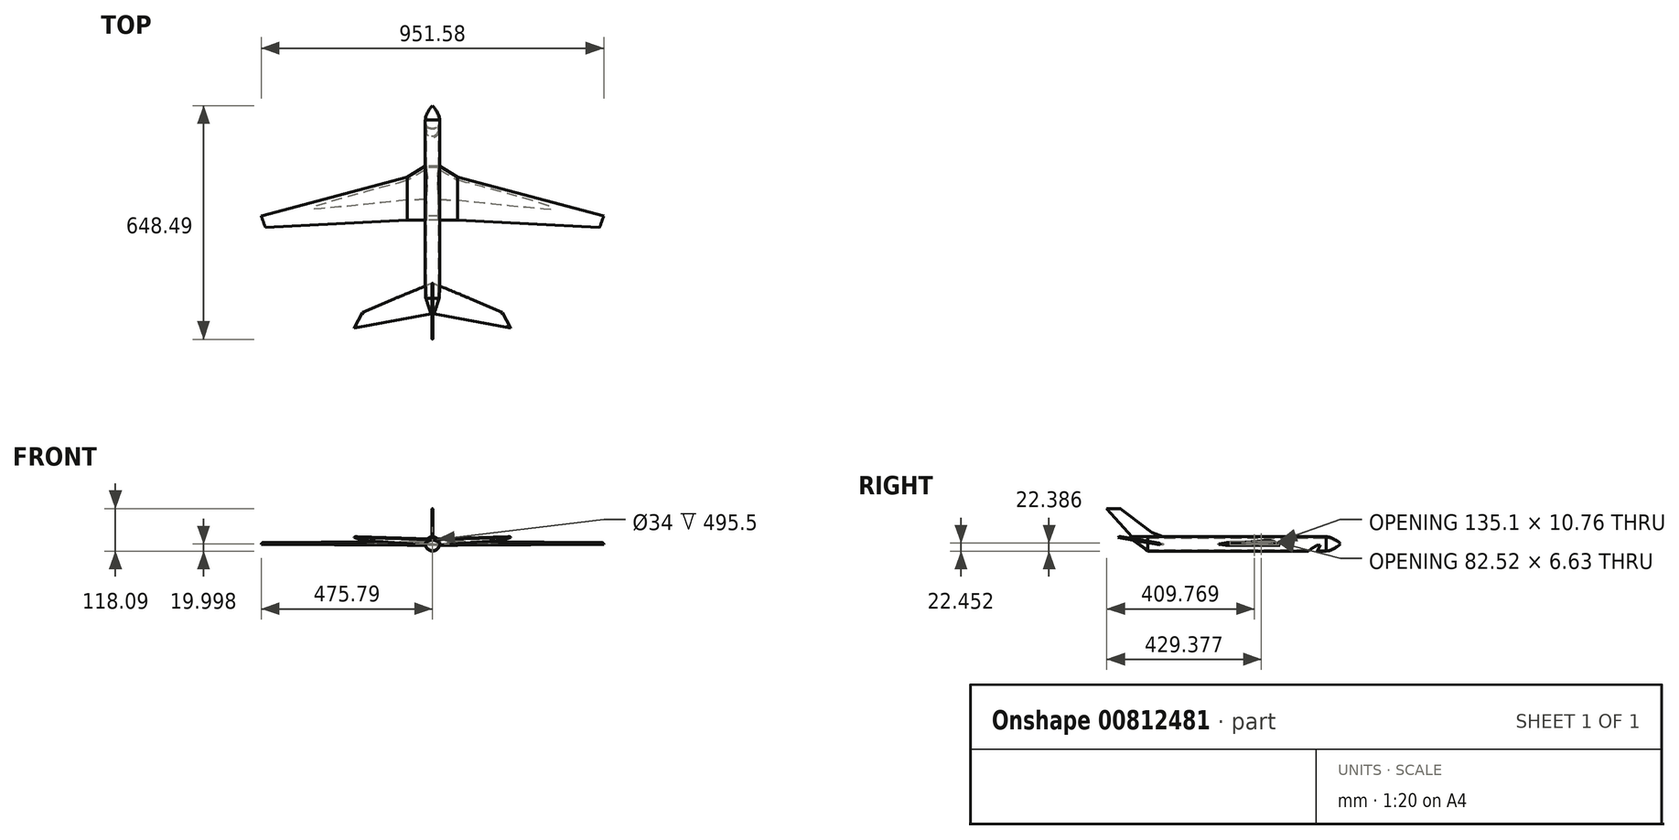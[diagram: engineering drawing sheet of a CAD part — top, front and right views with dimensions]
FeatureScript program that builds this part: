
annotation { "Feature Type Name" : "Feature", "Feature Type Description" : "" }
export const myFeature = defineFeature(function(context is Context, id is Id, definition is map)
    precondition{}
    {
        {
            var Q0;
            Q0=qCreatedBy(makeId("Top.planeOp"),FACE);
            var sketch = newSketch(context, id + "F0", { "sketchPlane" : qUnion([Q0])});
            skLineSegment(sketch, "E0", {"start": v(-55.98, -74.75) * mm, "end": v(71.16, -74.75) * mm, "construction": true});
            skSolve(sketch);
        }
        {
            var Q0;
            Q0=qCreatedBy(makeId("Right.planeOp"),FACE);
            var sketch = newSketch(context, id + "F1", { "sketchPlane" : qUnion([Q0])});
            skLineSegment(sketch, "E1", {"start": v(74.79, 0) * mm, "end": v(-74.95, 0) * mm});
            skFitSpline(sketch, "E2", {"points": [v(74.79, 0) * mm, v(48.12, 12.32) * mm, v(-21.53, 5.53) * mm, v(-74.95, 0) * mm], "startDerivative": vector(-92.28, 71.34) * mm, "endDerivative": vector(-103.51, -27.3) * mm});
            skSolve(sketch);
        }
        {
            var Q0;
            Q0=qCreatedBy(makeId("Right.planeOp"),FACE);
            cPlane(context, id + "F2", {"entities" : qUnion([Q0]), "cplaneType" : CPlaneType.OFFSET, "offset" : 50 * mm, "width" : 150 * mm, "height" : 150 * mm});
        }
        {
            var Q0;
            Q0=qCreatedBy(makeId("Right.planeOp"),FACE);
            cPlane(context, id + "F3", {"entities" : qUnion([Q0]), "cplaneType" : CPlaneType.OFFSET, "offset" : 50 * mm, "oppositeDirection" : true, "width" : 150 * mm, "height" : 150 * mm});
        }
        {
            var Q0;
            Q0=qCreatedBy(makeId("Top.planeOp"),FACE);
            var Q1;
            Q1=sQuery(id+"F0.wireOp",EDGE,"E0");
            cPlane(context, id + "F4", {"entities" : qUnion([Q0, Q1]), "cplaneType" : CPlaneType.LINE_ANGLE, "offset" : 25 * mm, "angle" : 90 * degree, "width" : 150 * mm, "height" : 150 * mm});
        }
        {
            var Q0;
            Q0=qCreatedBy(id+"F3.planeOp",FACE);
            var sketch = newSketch(context, id + "F5", { "sketchPlane" : qUnion([Q0])});
            skLineSegment(sketch, "E3", {"start": v(45.24, 0) * mm, "end": v(-74.75, 0) * mm});
            skFitSpline(sketch, "E4", {"points": [v(45.24, 0) * mm, v(23.7, 10.28) * mm, v(-25.4, 5.25) * mm, v(-74.75, 0) * mm], "startDerivative": vector(-70.78, 62.4) * mm, "endDerivative": vector(-207.75, -44.81) * mm});
            skSolve(sketch);
        }
        {
            var Q0;
            Q0=qCreatedBy(id+"F2.planeOp",FACE);
            var sketch = newSketch(context, id + "F6", { "sketchPlane" : qUnion([Q0])});
            skLineSegment(sketch, "E5", {"start": v(-30.59, 64.71) * mm, "end": v(-30.59, 8.46) * mm});
            skSolve(sketch);
        }
        {
            var Q0;
            Q0=sQuery(id+"F6.wireOp",EDGE,"E5");
            var Q1;
            Q1=qCreatedBy(id+"F2.planeOp",FACE);
            cPlane(context, id + "F7", {"entities" : qUnion([Q0, Q1]), "cplaneType" : CPlaneType.LINE_ANGLE, "offset" : 25 * mm, "angle" : 180 * degree, "width" : 150 * mm, "height" : 150 * mm});
        }
        {
            var Q0;
            Q0=qCreatedBy(id+"F7.planeOp",FACE);
            var sketch = newSketch(context, id + "F8", { "sketchPlane" : qUnion([Q0])});
            skLineSegment(sketch, "E6", {"start": v(45.24, 0) * mm, "end": v(-74.75, 0) * mm});
            skFitSpline(sketch, "E7", {"points": [v(45.24, 0) * mm, v(23.7, 10.28) * mm, v(-25.4, 5.25) * mm, v(-74.75, 0) * mm], "startDerivative": vector(-70.78, 62.4) * mm, "endDerivative": vector(-207.75, -44.81) * mm});
            skSolve(sketch);
        }
        {
            var Q0;
            Q0=qCreatedBy(id+"F3.planeOp",FACE);
            cPlane(context, id + "F9", {"entities" : qUnion([Q0]), "cplaneType" : CPlaneType.OFFSET, "offset" : 517 * mm, "width" : 150 * mm, "height" : 150 * mm});
        }
        {
            var Q0;
            Q0=qCreatedBy(id+"F9.planeOp",FACE);
            var sketch = newSketch(context, id + "F10", { "sketchPlane" : qUnion([Q0])});
            skLineSegment(sketch, "E8", {"start": v(-31.76, 27.94) * mm, "end": v(-31.76, -39.12) * mm});
            skSolve(sketch);
        }
        {
            var Q0;
            Q0=qCreatedBy(id+"F3.planeOp",FACE);
            cPlane(context, id + "F11", {"entities" : qUnion([Q0]), "cplaneType" : CPlaneType.OFFSET, "offset" : 417 * mm, "oppositeDirection" : true, "width" : 150 * mm, "height" : 150 * mm});
        }
        {
            var Q0;
            Q0=qCreatedBy(id+"F11.planeOp",FACE);
            var sketch = newSketch(context, id + "F12", { "sketchPlane" : qUnion([Q0])});
            skLineSegment(sketch, "E9", {"start": v(-31.76, 27.94) * mm, "end": v(-31.76, -39.12) * mm});
            skSolve(sketch);
        }
        {
            var Q0;
            Q0=qCreatedBy(id+"F11.planeOp",FACE);
            var Q1;
            Q1=sQuery(id+"F12.wireOp",EDGE,"E9");
            cPlane(context, id + "F13", {"entities" : qUnion([Q0, Q1]), "cplaneType" : CPlaneType.LINE_ANGLE, "offset" : 25 * mm, "angle" : 20 * degree, "oppositeDirection" : true, "width" : 150 * mm, "height" : 150 * mm});
        }
        {
            var Q0;
            Q0=qCreatedBy(id+"F13.planeOp",FACE);
            var sketch = newSketch(context, id + "F14", { "sketchPlane" : qUnion([Q0])});
            skLineSegment(sketch, "E10", {"start": v(-62.42, 3.13) * mm, "end": v(-97.1, 3.13) * mm});
            skFitSpline(sketch, "E11", {"points": [v(-97.1, 3.13) * mm, v(-87.9, 7.01) * mm, v(-75.05, 5.07) * mm, v(-62.42, 3.13) * mm], "startDerivative": vector(19.92, 21.32) * mm, "endDerivative": vector(25.74, -8.08) * mm});
            skSolve(sketch);
        }
        {
            var Q0;
            Q0=sQuery(id+"F10.wireOp",EDGE,"E8");
            var Q1;
            Q1=qCreatedBy(id+"FuSxjUWaqpYeULK_0.planeOp",FACE);
            cPlane(context, id + "F15", {"entities" : qUnion([Q0, Q1]), "cplaneType" : CPlaneType.LINE_ANGLE, "offset" : 90 * mm, "angle" : 90 * degree, "width" : 150 * mm, "height" : 150 * mm});
        }
        {
            var Q0;
            Q0=qCreatedBy(id+"F15.planeOp",FACE);
            var Q1;
            Q1=sQuery(id+"F10.wireOp",EDGE,"E8");
            cPlane(context, id + "F16", {"entities" : qUnion([Q0, Q1]), "cplaneType" : CPlaneType.LINE_ANGLE, "offset" : 25 * mm, "angle" : 250 * degree, "oppositeDirection" : true, "width" : 150 * mm, "height" : 150 * mm});
        }
        {
            var Q0;
            Q0=qCreatedBy(makeId("Top.planeOp"),FACE);
            var sketch = newSketch(context, id + "F17", { "sketchPlane" : qUnion([Q0])});
            skLineSegment(sketch, "E12", {"start": v(-443.93, -95.15) * mm, "end": v(0, -95.15) * mm, "construction": true});
            skLineSegment(sketch, "E13.MirrorCS", {"start": v(443.93, -95.15) * mm, "end": v(0, -95.15) * mm, "construction": true});
            skLineSegment(sketch, "E14", {"start": v(-455.79, -62.57) * mm, "end": v(0, -62.57) * mm, "construction": true});
            skLineSegment(sketch, "E15.MirrorCS", {"start": v(455.79, -62.57) * mm, "end": v(0, -62.57) * mm, "construction": true});
            skLineSegment(sketch, "E16", {"start": v(-455.79, -62.57) * mm, "end": v(-443.93, -95.15) * mm});
            skLineSegment(sketch, "E17.MirrorCS", {"start": v(455.79, -62.57) * mm, "end": v(443.93, -95.15) * mm, "construction": true});
            skLineSegment(sketch, "E18.MirrorCS", {"start": v(-455.79, -62.57) * mm, "end": v(-443.93, -95.15) * mm, "construction": true});
            skSolve(sketch);
        }
        {
            var Q0;
            Q0=qCreatedBy(makeId("Top.planeOp"),FACE);
            cPlane(context, id + "F18", {"entities" : qUnion([Q0]), "cplaneType" : CPlaneType.OFFSET, "offset" : 3.13 * mm, "width" : 150 * mm, "height" : 150 * mm});
        }
        {
            var Q0;
            Q0=qCreatedBy(id+"F18.planeOp",FACE);
            var sketch = newSketch(context, id + "F19", { "sketchPlane" : qUnion([Q0])});
            skLineSegment(sketch, "E19", {"start": v(443.93, -95.15) * mm, "end": v(455.79, -62.57) * mm});
            skSolve(sketch);
        }
        {
            var Q0;
            Q0=qCreatedBy(id+"F16.planeOp",FACE);
            var sketch = newSketch(context, id + "F20", { "sketchPlane" : qUnion([Q0])});
            skLineSegment(sketch, "E20", {"start": v(-112.36, -6.7) * mm, "end": v(-147.03, -6.7) * mm});
            skFitSpline(sketch, "E21", {"points": [v(-97.1, 3.13) * mm, v(-87.9, 7.01) * mm, v(-75.05, 5.07) * mm, v(-62.42, 3.13) * mm], "startDerivative": vector(19.92, 21.32) * mm, "endDerivative": vector(25.74, -8.08) * mm});
            skLineSegment(sketch, "E22", {"start": v(-62.42, 3.13) * mm, "end": v(-97.1, 3.13) * mm});
            skSolve(sketch);
        }
        {
            var Q0;
            Q0=makeQuery(id+"F1.imprint","IMPRINT",FACE,{"disambiguationData":[TD([[makeQuery(id+"F1.imprint","IMPRINT",EDGE,{"derivedFrom":sQuery(id+"F1.wireOp",EDGE,"E1")}),-1.0]])]});
            var Q1;
            Q1=makeQuery(id+"F5.imprint","IMPRINT",FACE,{"disambiguationData":[TD([[makeQuery(id+"F5.imprint","IMPRINT",EDGE,{"derivedFrom":sQuery(id+"F5.wireOp",EDGE,"E3")}),-1.0]])]});
            loft(context, id + "F21", {"sheetProfilesArray" : [{ "sheetProfileEntities" : qUnion([Q0]) }, { "sheetProfileEntities" : qUnion([Q1]) }]});
        }
        {
            var Q1;
            Q1=makeQuery(id+"F21.opLoft","CAP_FACE",FACE,{"disambiguationData":[OSD([makeQuery(id+"F5.imprint","IMPRINT",FACE,{"disambiguationData":[TD([[makeQuery(id+"F5.imprint","IMPRINT",EDGE,{"derivedFrom":sQuery(id+"F5.wireOp",EDGE,"E3")}),-1.0]])]})])],"isStart":true});
            var Q2;
            Q2=makeQuery(id+"F14.imprint","IMPRINT",FACE,{"disambiguationData":[TD([[makeQuery(id+"F14.imprint","IMPRINT",EDGE,{"derivedFrom":sQuery(id+"F14.wireOp",EDGE,"E10")}),-1.0]])]});
            loft(context, id + "F22", {"operationType" : NewBodyOperationType.ADD, "sheetProfilesArray" : [{ "sheetProfileEntities" : qUnion([Q1]) }, { "sheetProfileEntities" : qUnion([Q2]) }]});
        }
        {
            var Q0;
            Q0=makeQuery(id+"F21.opLoft","SWEPT_BODY",BODY,{"disambiguationData":[OSD([makeQuery(id+"F1.imprint","IMPRINT",FACE,{"disambiguationData":[TD([[makeQuery(id+"F1.imprint","IMPRINT",EDGE,{"derivedFrom":sQuery(id+"F1.wireOp",EDGE,"E1")}),-1.0]])]}),makeQuery(id+"F5.imprint","IMPRINT",FACE,{"disambiguationData":[TD([[makeQuery(id+"F5.imprint","IMPRINT",EDGE,{"derivedFrom":sQuery(id+"F5.wireOp",EDGE,"E3")}),-1.0]])]})])]});
            transform(context, id + "F23", {"entities" : qUnion([Q0]), "transformType" : TransformType.TRANSLATION_3D, "dx" : -20 * mm, "dy" : 0 * mm, "dz" : 0 * mm, "makeCopy" : false});
        }
        {
            var Q0;
            Q0=makeQuery(id+"F1.imprint","IMPRINT",FACE,{"disambiguationData":[TD([[makeQuery(id+"F1.imprint","IMPRINT",EDGE,{"derivedFrom":sQuery(id+"F1.wireOp",EDGE,"E1")}),-1.0]])]});
            var Q1;
            Q1=makeQuery(id+"F8.imprint","IMPRINT",FACE,{"disambiguationData":[TD([[makeQuery(id+"F8.imprint","IMPRINT",EDGE,{"derivedFrom":sQuery(id+"F8.wireOp",EDGE,"E6")}),-1.0]])]});
            loft(context, id + "F24", {"sheetProfilesArray" : [{ "sheetProfileEntities" : qUnion([Q0]) }, { "sheetProfileEntities" : qUnion([Q1]) }]});
        }
        {
            var Q1;
            Q1=makeQuery(id+"F24.opLoft","CAP_FACE",FACE,{"disambiguationData":[OSD([makeQuery(id+"F8.imprint","IMPRINT",FACE,{"disambiguationData":[TD([[makeQuery(id+"F8.imprint","IMPRINT",EDGE,{"derivedFrom":sQuery(id+"F8.wireOp",EDGE,"E6")}),-1.0]])]})])],"isStart":true});
            var Q2;
            Q2=makeQuery(id+"F20.imprint","IMPRINT",FACE,{"disambiguationData":[TD([[makeQuery(id+"F20.imprint","IMPRINT",EDGE,{"derivedFrom":sQuery(id+"F20.wireOp",EDGE,"E21")}),-1.0]])]});
            loft(context, id + "F25", {"operationType" : NewBodyOperationType.ADD, "sheetProfilesArray" : [{ "sheetProfileEntities" : qUnion([Q1]) }, { "sheetProfileEntities" : qUnion([Q2]) }]});
        }
        {
            var Q0;
            Q0=makeQuery(id+"F24.opLoft","SWEPT_BODY",BODY,{"disambiguationData":[OSD([makeQuery(id+"F1.imprint","IMPRINT",FACE,{"disambiguationData":[TD([[makeQuery(id+"F1.imprint","IMPRINT",EDGE,{"derivedFrom":sQuery(id+"F1.wireOp",EDGE,"E1")}),-1.0]])]}),makeQuery(id+"F8.imprint","IMPRINT",FACE,{"disambiguationData":[TD([[makeQuery(id+"F8.imprint","IMPRINT",EDGE,{"derivedFrom":sQuery(id+"F8.wireOp",EDGE,"E6")}),-1.0]])]})])]});
            transform(context, id + "F26", {"entities" : qUnion([Q0]), "transformType" : TransformType.TRANSLATION_3D, "dx" : 20 * mm, "dy" : 0 * mm, "dz" : 0 * mm, "makeCopy" : false});
        }
        {
            var Q0;
            Q0=makeQuery(id+"F21.opLoft","CAP_FACE",FACE,{"disambiguationData":[OSD([makeQuery(id+"F1.imprint","IMPRINT",FACE,{"disambiguationData":[TD([[makeQuery(id+"F1.imprint","IMPRINT",EDGE,{"derivedFrom":sQuery(id+"F1.wireOp",EDGE,"E1")}),-1.0]])]})])],"isStart":true});
            var Q1;
            Q1=makeQuery(id+"F24.opLoft","CAP_FACE",FACE,{"disambiguationData":[OSD([makeQuery(id+"F1.imprint","IMPRINT",FACE,{"disambiguationData":[TD([[makeQuery(id+"F1.imprint","IMPRINT",EDGE,{"derivedFrom":sQuery(id+"F1.wireOp",EDGE,"E1")}),-1.0]])]})])],"isStart":true});
            var Q2;
            Q2=makeQuery(id+"F22.opLoft","CAP_FACE",FACE,{"disambiguationData":[OSD([makeQuery(id+"F14.imprint","IMPRINT",FACE,{"disambiguationData":[TD([[makeQuery(id+"F14.imprint","IMPRINT",EDGE,{"derivedFrom":sQuery(id+"F14.wireOp",EDGE,"E10")}),-1.0]])]})])],"isStart":true});
            var Q3;
            Q3=makeQuery(id+"F25.opLoft","CAP_FACE",FACE,{"disambiguationData":[OSD([makeQuery(id+"F20.imprint","IMPRINT",FACE,{"disambiguationData":[TD([[makeQuery(id+"F20.imprint","IMPRINT",EDGE,{"derivedFrom":sQuery(id+"F20.wireOp",EDGE,"E21")}),-1.0]])]})])],"isStart":true});
            shell(context, id + "F27", {"entities" : qUnion([Q0, Q1, Q2, Q3]), "thickness" : 3 * mm});
        }
        {
            var Q0;
            Q0=qCreatedBy(makeId("Right.planeOp"),FACE);
            cPlane(context, id + "F28", {"entities" : qUnion([Q0]), "cplaneType" : CPlaneType.OFFSET, "offset" : 20 * mm, "width" : 150 * mm, "height" : 150 * mm});
        }
        {
            var Q0;
            Q0=qCreatedBy(id+"F28.planeOp",FACE);
            var sketch = newSketch(context, id + "F29", { "sketchPlane" : qUnion([Q0])});
            skLineSegment(sketch, "E23", {"start": v(74.79, 0) * mm, "end": v(-74.95, 0) * mm});
            skFitSpline(sketch, "E24", {"points": [v(74.79, 0) * mm, v(48.12, 12.32) * mm, v(-21.53, 5.53) * mm, v(-74.95, 0) * mm], "startDerivative": vector(-92.28, 71.34) * mm, "endDerivative": vector(-103.51, -27.3) * mm});
            skSolve(sketch);
        }
        {
            var Q0;
            Q0=qCreatedBy(makeId("Right.planeOp"),FACE);
            cPlane(context, id + "F30", {"entities" : qUnion([Q0]), "cplaneType" : CPlaneType.OFFSET, "offset" : 20 * mm, "oppositeDirection" : true, "width" : 150 * mm, "height" : 150 * mm});
        }
        {
            var Q0;
            Q0=qCreatedBy(id+"F30.planeOp",FACE);
            var sketch = newSketch(context, id + "F31", { "sketchPlane" : qUnion([Q0])});
            skLineSegment(sketch, "E25", {"start": v(74.79, 0) * mm, "end": v(-74.95, 0) * mm});
            skFitSpline(sketch, "E26", {"points": [v(74.79, 0) * mm, v(48.12, 12.32) * mm, v(-21.53, 5.53) * mm, v(-74.95, 0) * mm], "startDerivative": vector(-92.28, 71.34) * mm, "endDerivative": vector(-103.51, -27.3) * mm});
            skSolve(sketch);
        }
        {
            var Q1;
            Q1 = qSketchRegion(id + "F29", true);
            var Q2;
            Q2 = qSketchRegion(id + "F31", true);
            loft(context, id + "F32", {"sheetProfilesArray" : [{ "sheetProfileEntities" : qUnion([Q1]) }, { "sheetProfileEntities" : qUnion([Q2]) }]});
        }
        {
            var Q0;
            Q0=makeQuery(id+"F32.opLoft","CAP_FACE",FACE,{"disambiguationData":[OSD([makeQuery(id+"F29.imprint","IMPRINT",FACE,{"disambiguationData":[TD([[makeQuery(id+"F29.imprint","IMPRINT",EDGE,{"derivedFrom":sQuery(id+"F29.wireOp",EDGE,"E23")}),-1.0]])]})])],"isStart":true});
            var Q1;
            Q1=makeQuery(id+"F32.opLoft","CAP_FACE",FACE,{"disambiguationData":[OSD([makeQuery(id+"F31.imprint","IMPRINT",FACE,{"disambiguationData":[TD([[makeQuery(id+"F31.imprint","IMPRINT",EDGE,{"derivedFrom":sQuery(id+"F31.wireOp",EDGE,"E25")}),-1.0]])]})])],"isStart":true});
            shell(context, id + "F33", {"entities" : qUnion([Q0, Q1]), "thickness" : 1 * mm});
        }
        {
            var Q0;
            Q0=qCreatedBy(makeId("Front.planeOp"),FACE);
            var sketch = newSketch(context, id + "F34", { "sketchPlane" : qUnion([Q0])});
            skCircle(sketch, "E27", {"center": v(0, 3.93) * mm, "radius": 20 * mm});
            skSolve(sketch);
        }
        {
            var Q0;
            Q0 = qSketchRegion(id + "F34", true);
            extrude(context, id + "F35", {"entities" : qUnion([Q0]), "depth" : 266 * mm, "offsetDistance" : 25 * mm, "hasSecondDirection" : true, "secondDirectionOppositeDirection" : true, "secondDirectionDepth" : 229.5 * mm});
        }
        {
            var Q0;
            Q0=makeQuery(id+"F35.opExtrude","CAP_FACE",FACE,{"disambiguationData":[OSD([sQuery(id+"F34.wireOp",EDGE,"E27")])],"isStart":true});
            cPlane(context, id + "F36", {"entities" : qUnion([Q0]), "cplaneType" : CPlaneType.OFFSET, "offset" : 49 * mm, "width" : 150 * mm, "height" : 150 * mm});
        }
        {
            var Q0;
            Q0=makeQuery(id+"F35.opExtrude","CAP_FACE",FACE,{"disambiguationData":[OSD([sQuery(id+"F34.wireOp",EDGE,"E27")])],"isStart":false});
            cPlane(context, id + "F37", {"entities" : qUnion([Q0]), "cplaneType" : CPlaneType.OFFSET, "offset" : 44 * mm, "width" : 150 * mm, "height" : 150 * mm});
        }
        {
            var Q0;
            Q0=qCreatedBy(id+"F37.planeOp",FACE);
            var sketch = newSketch(context, id + "F38", { "sketchPlane" : qUnion([Q0])});
            skCircle(sketch, "E28", {"center": v(0, 20.66) * mm, "radius": 4 * mm});
            skSolve(sketch);
        }
        {
            var Q0;
            Q0=makeQuery(id+"F35.opExtrude","CAP_FACE",FACE,{"disambiguationData":[OSD([sQuery(id+"F34.wireOp",EDGE,"E27")])],"isStart":true});
            cPlane(context, id + "F39", {"entities" : qUnion([Q0]), "cplaneType" : CPlaneType.OFFSET, "offset" : 0 * mm, "width" : 150 * mm, "height" : 150 * mm});
        }
        {
            var Q0;
            Q0=makeQuery(id+"F35.opExtrude","CAP_FACE",FACE,{"disambiguationData":[OSD([sQuery(id+"F34.wireOp",EDGE,"E27")])],"isStart":false});
            cPlane(context, id + "F40", {"entities" : qUnion([Q0]), "cplaneType" : CPlaneType.OFFSET, "offset" : 0 * mm, "width" : 150 * mm, "height" : 150 * mm});
        }
        {
            var Q0;
            Q0=makeQuery(id+"F35.opExtrude","CAP_FACE",FACE,{"disambiguationData":[OSD([sQuery(id+"F34.wireOp",EDGE,"E27")])],"isStart":true});
            var Q1;
            Q1=makeQuery(id+"F35.opExtrude","CAP_FACE",FACE,{"disambiguationData":[OSD([sQuery(id+"F34.wireOp",EDGE,"E27")])],"isStart":false});
            shell(context, id + "F41", {"entities" : qUnion([Q0, Q1]), "thickness" : 3 * mm});
        }
        {
            var Q0;
            Q0=qCreatedBy(id+"F39.planeOp",FACE);
            var sketch = newSketch(context, id + "F42", { "sketchPlane" : qUnion([Q0])});
            skCircle(sketch, "E29", {"center": v(0, 3.93) * mm, "radius": 20 * mm});
            skSolve(sketch);
        }
        {
            var Q0;
            Q0=qCreatedBy(id+"F36.planeOp",FACE);
            var sketch = newSketch(context, id + "F43", { "sketchPlane" : qUnion([Q0])});
            skCircle(sketch, "E30", {"center": v(0, 4.07) * mm, "radius": 20 * mm});
            skLineSegment(sketch, "E31", {"start": v(0, 4.07) * mm, "end": v(0, 32.13) * mm});
            skLineSegment(sketch, "E32", {"start": v(0, 32.13) * mm, "end": v(0, -30.37) * mm});
            skSolve(sketch);
        }
        {
            var Q0;
            Q0=sQuery(id+"F43.wireOp",EDGE,"E32");
            var Q1;
            Q1=qCreatedBy(id+"F36.planeOp",FACE);
            cPlane(context, id + "F44", {"entities" : qUnion([Q0, Q1]), "cplaneType" : CPlaneType.LINE_ANGLE, "offset" : 25 * mm, "angle" : 90 * degree, "width" : 150 * mm, "height" : 150 * mm});
        }
        {
            var Q0;
            Q0=qCreatedBy(id+"F44.planeOp",FACE);
            var sketch = newSketch(context, id + "F45", { "sketchPlane" : qUnion([Q0])});
            skLineSegment(sketch, "E33", {"start": v(-269.69, 3.9) * mm, "end": v(-200.95, 3.97) * mm});
            skFitSpline(sketch, "E34", {"points": [v(-229.5, 23.81) * mm, v(-247.18, 19.64) * mm, v(-269.69, 3.9) * mm], "startDerivative": vector(-73.62, -3.54) * mm, "endDerivative": vector(-27.59, -37.58) * mm});
            skFitSpline(sketch, "E35", {"points": [v(-229.51, 20.75) * mm, v(-245.48, 17.05) * mm, v(-265.25, 3.9) * mm], "startDerivative": vector(-69.48, -5) * mm, "endDerivative": vector(-21.83, -31.1) * mm});
            skLineSegment(sketch, "E36", {"start": v(-229.5, 23.81) * mm, "end": v(-229.51, 20.75) * mm});
            skSolve(sketch);
        }
        {
            var Q0;
            Q0=qCreatedBy(id+"F40.planeOp",FACE);
            var sketch = newSketch(context, id + "F46", { "sketchPlane" : qUnion([Q0])});
            skCircle(sketch, "E37", {"center": v(0, 3.93) * mm, "radius": 20 * mm});
            skSolve(sketch);
        }
        {
            var Q1;
            Q1=makeQuery(id+"F46.imprint","IMPRINT",FACE,{"disambiguationData":[TD([[makeQuery(id+"F46.imprint","IMPRINT",EDGE,{"derivedFrom":sQuery(id+"F46.wireOp",EDGE,"E37")}),1.0]])]});
            var Q2;
            Q2=makeQuery(id+"F38.imprint","IMPRINT",FACE,{"disambiguationData":[TD([[makeQuery(id+"F38.imprint","IMPRINT",EDGE,{"derivedFrom":sQuery(id+"F38.wireOp",EDGE,"E28")}),1.0]])]});
            loft(context, id + "F47", {"sheetProfilesArray" : [{ "sheetProfileEntities" : qUnion([Q1]) }, { "sheetProfileEntities" : qUnion([Q2]) }]});
        }
        {
            var Q0;
            Q0=makeQuery(id+"F35.opExtrude","SWEPT_BODY",BODY,{"disambiguationData":[OSD([sQuery(id+"F34.wireOp",EDGE,"E27")])]});
            var Q1;
            Q1=makeQuery(id+"F47.opLoft","SWEPT_BODY",BODY,{"disambiguationData":[OSD([makeQuery(id+"F38.imprint","IMPRINT",FACE,{"disambiguationData":[TD([[makeQuery(id+"F38.imprint","IMPRINT",EDGE,{"derivedFrom":sQuery(id+"F38.wireOp",EDGE,"E28")}),1.0]])]}),makeQuery(id+"F46.imprint","IMPRINT",FACE,{"disambiguationData":[TD([[makeQuery(id+"F46.imprint","IMPRINT",EDGE,{"derivedFrom":sQuery(id+"F46.wireOp",EDGE,"E37")}),1.0]])]})])]});
            transform(context, id + "F48", {"entities" : qUnion([Q0, Q1]), "transformType" : TransformType.TRANSLATION_3D, "dx" : 0 * mm, "dy" : -25 * mm, "dz" : 0 * mm, "makeCopy" : false});
        }
        {
            var Q0;
            Q0=makeQuery(id+"F21.opLoft","SWEPT_BODY",BODY,{"disambiguationData":[OSD([makeQuery(id+"F1.imprint","IMPRINT",FACE,{"disambiguationData":[TD([[makeQuery(id+"F1.imprint","IMPRINT",EDGE,{"derivedFrom":sQuery(id+"F1.wireOp",EDGE,"E1")}),-1.0]])]}),makeQuery(id+"F5.imprint","IMPRINT",FACE,{"disambiguationData":[TD([[makeQuery(id+"F5.imprint","IMPRINT",EDGE,{"derivedFrom":sQuery(id+"F5.wireOp",EDGE,"E3")}),-1.0]])]})])]});
            var Q1;
            Q1=makeQuery(id+"F24.opLoft","SWEPT_BODY",BODY,{"disambiguationData":[OSD([makeQuery(id+"F1.imprint","IMPRINT",FACE,{"disambiguationData":[TD([[makeQuery(id+"F1.imprint","IMPRINT",EDGE,{"derivedFrom":sQuery(id+"F1.wireOp",EDGE,"E1")}),-1.0]])]}),makeQuery(id+"F8.imprint","IMPRINT",FACE,{"disambiguationData":[TD([[makeQuery(id+"F8.imprint","IMPRINT",EDGE,{"derivedFrom":sQuery(id+"F8.wireOp",EDGE,"E6")}),-1.0]])]})])]});
            var Q2;
            Q2=makeQuery(id+"F32.opLoft","SWEPT_BODY",BODY,{"disambiguationData":[OSD([makeQuery(id+"F29.imprint","IMPRINT",FACE,{"disambiguationData":[TD([[makeQuery(id+"F29.imprint","IMPRINT",EDGE,{"derivedFrom":sQuery(id+"F29.wireOp",EDGE,"E23")}),-1.0]])]}),makeQuery(id+"F31.imprint","IMPRINT",FACE,{"disambiguationData":[TD([[makeQuery(id+"F31.imprint","IMPRINT",EDGE,{"derivedFrom":sQuery(id+"F31.wireOp",EDGE,"E25")}),-1.0]])]})])]});
            transform(context, id + "F49", {"entities" : qUnion([Q0, Q1, Q2]), "transformType" : TransformType.TRANSLATION_3D, "dx" : 473 * mm, "dy" : -213 * mm, "dz" : 0 * mm, "makeCopy" : false});
        }
        {
            var Q0;
            Q0=qCreatedBy(id+"F28.planeOp",FACE);
            cPlane(context, id + "F50", {"entities" : qUnion([Q0]), "cplaneType" : CPlaneType.OFFSET, "offset" : 6 * mm, "width" : 150 * mm, "height" : 150 * mm});
        }
        {
            var Q0;
            Q0=qCreatedBy(id+"F50.planeOp",FACE);
            var sketch = newSketch(context, id + "F51", { "sketchPlane" : qUnion([Q0])});
            skLineSegment(sketch, "E38", {"start": v(74.98, 0) * mm, "end": v(-75.4, 0) * mm});
            skFitSpline(sketch, "E39", {"points": [v(74.98, 0) * mm, v(48.19, 12.47) * mm, v(-21.6, 6.14) * mm, v(-75.4, 0) * mm], "startDerivative": vector(-90.97, 72.73) * mm, "endDerivative": vector(-103.22, -28.45) * mm});
            skSolve(sketch);
        }
        {
            var Q0;
            Q0 = qSketchRegion(id + "F51", true);
            extrude(context, id + "F52", {"entities" : qUnion([Q0]), "operationType" : NewBodyOperationType.REMOVE, "oppositeDirection" : true, "depth" : 80 * mm, "offsetDistance" : 25 * mm});
        }
        {
            var Q0;
            Q0=makeQuery(id+"F21.opLoft","SWEPT_BODY",BODY,{"disambiguationData":[OSD([makeQuery(id+"F1.imprint","IMPRINT",FACE,{"disambiguationData":[TD([[makeQuery(id+"F1.imprint","IMPRINT",EDGE,{"derivedFrom":sQuery(id+"F1.wireOp",EDGE,"E1")}),-1.0]])]}),makeQuery(id+"F5.imprint","IMPRINT",FACE,{"disambiguationData":[TD([[makeQuery(id+"F5.imprint","IMPRINT",EDGE,{"derivedFrom":sQuery(id+"F5.wireOp",EDGE,"E3")}),-1.0]])]})])]});
            var Q1;
            Q1=makeQuery(id+"F24.opLoft","SWEPT_BODY",BODY,{"disambiguationData":[OSD([makeQuery(id+"F1.imprint","IMPRINT",FACE,{"disambiguationData":[TD([[makeQuery(id+"F1.imprint","IMPRINT",EDGE,{"derivedFrom":sQuery(id+"F1.wireOp",EDGE,"E1")}),-1.0]])]}),makeQuery(id+"F8.imprint","IMPRINT",FACE,{"disambiguationData":[TD([[makeQuery(id+"F8.imprint","IMPRINT",EDGE,{"derivedFrom":sQuery(id+"F8.wireOp",EDGE,"E6")}),-1.0]])]})])]});
            var Q2;
            Q2=makeQuery(id+"F32.opLoft","SWEPT_BODY",BODY,{"disambiguationData":[OSD([makeQuery(id+"F29.imprint","IMPRINT",FACE,{"disambiguationData":[TD([[makeQuery(id+"F29.imprint","IMPRINT",EDGE,{"derivedFrom":sQuery(id+"F29.wireOp",EDGE,"E23")}),-1.0]])]}),makeQuery(id+"F31.imprint","IMPRINT",FACE,{"disambiguationData":[TD([[makeQuery(id+"F31.imprint","IMPRINT",EDGE,{"derivedFrom":sQuery(id+"F31.wireOp",EDGE,"E25")}),-1.0]])]})])]});
            transform(context, id + "F53", {"entities" : qUnion([Q0, Q1, Q2]), "transformType" : TransformType.TRANSLATION_3D, "dx" : -69 * mm, "dy" : 0 * mm, "dz" : 306 * mm, "makeCopy" : false});
        }
        {
            var Q0;
            {var subQ0=sQuery(id+"F31.wireOp",EDGE,"E25");var subQ1=sQuery(id+"F31.wireOp",EDGE,"E26");var subQ2=sQuery(id+"F29.wireOp",EDGE,"E23");var subQ3=sQuery(id+"F29.wireOp",EDGE,"E24");Q0=makeQuery(id+"F32.opLoft","SWEPT_FACE",FACE,{"disambiguationData":[OSD([subQ2,subQ3,subQ0,subQ1]),TDD([makeQuery(id+"F29.imprint","INTERSECT",VERTEX,{"disambiguationData":[OD(0.0)],"derivedFrom":[subQ2,subQ3]}),makeQuery(id+"F29.imprint","INTERSECT",VERTEX,{"disambiguationData":[OD(1.0)],"derivedFrom":[subQ2,subQ3]}),makeQuery(id+"F29.imprint","IMPRINT",EDGE,{"derivedFrom":subQ2}),makeQuery(id+"F31.imprint","INTERSECT",VERTEX,{"disambiguationData":[OD(0.0)],"derivedFrom":[subQ0,subQ1]}),makeQuery(id+"F31.imprint","INTERSECT",VERTEX,{"disambiguationData":[OD(1.0)],"derivedFrom":[subQ0,subQ1]}),makeQuery(id+"F31.imprint","IMPRINT",EDGE,{"derivedFrom":subQ0})])]});}
            cPlane(context, id + "F54", {"entities" : qUnion([Q0]), "cplaneType" : CPlaneType.OFFSET, "offset" : 11 * mm, "width" : 150 * mm, "height" : 150 * mm});
        }
        {
            var Q0;
            Q0=qCreatedBy(id+"F37.planeOp",FACE);
            var sketch = newSketch(context, id + "F55", { "sketchPlane" : qUnion([Q0])});
            skLineSegment(sketch, "E40", {"start": v(0, -10.99) * mm, "end": v(0, 13.89) * mm});
            skLineSegment(sketch, "E41", {"start": v(-13.36, 10.5) * mm, "end": v(14.6, 10.5) * mm});
            skSolve(sketch);
        }
        {
            var Q0;
            Q0=qCreatedBy(id+"F37.planeOp",FACE);
            var Q1;
            Q1=sQuery(id+"F55.wireOp",EDGE,"E40");
            cPlane(context, id + "F56", {"entities" : qUnion([Q0, Q1]), "cplaneType" : CPlaneType.LINE_ANGLE, "offset" : 25 * mm, "angle" : 90 * degree, "width" : 150 * mm, "height" : 150 * mm});
        }
        {
            var Q0;
            Q0=qCreatedBy(id+"F56.planeOp",FACE);
            var sketch = newSketch(context, id + "F57", { "sketchPlane" : qUnion([Q0])});
            skLineSegment(sketch, "E42", {"start": v(335.03, 23.06) * mm, "end": v(405.2, 102.02) * mm});
            skLineSegment(sketch, "E43", {"start": v(405.2, 102.02) * mm, "end": v(367.35, 102.02) * mm});
            skLineSegment(sketch, "E44", {"start": v(249.27, 24.2) * mm, "end": v(290.93, 24.2) * mm});
            skLineSegment(sketch, "E45", {"start": v(290.93, 24.2) * mm, "end": v(291.81, 22.53) * mm});
            skLineSegment(sketch, "E46", {"start": v(291.81, 22.53) * mm, "end": v(334.88, 22.53) * mm});
            skLineSegment(sketch, "E47", {"start": v(334.88, 22.53) * mm, "end": v(335.03, 23.06) * mm});
            skLineSegment(sketch, "E48", {"start": v(367.35, 102.02) * mm, "end": v(290.68, 42.68) * mm});
            skLineSegment(sketch, "E49", {"start": v(290.68, 42.68) * mm, "end": v(280.1, 35.62) * mm});
            skLineSegment(sketch, "E50", {"start": v(280.1, 35.62) * mm, "end": v(249.27, 24.2) * mm});
            skSolve(sketch);
        }
        {
            var Q0;
            Q0=makeQuery(id+"F47.opLoft","CAP_FACE",FACE,{"disambiguationData":[OSD([makeQuery(id+"F46.imprint","IMPRINT",FACE,{"disambiguationData":[TD([[makeQuery(id+"F46.imprint","IMPRINT",EDGE,{"derivedFrom":sQuery(id+"F46.wireOp",EDGE,"E37")}),1.0]])]})])],"isStart":true});
            var Q1;
            Q1=makeQuery(id+"F47.opLoft","CAP_FACE",FACE,{"disambiguationData":[OSD([makeQuery(id+"F38.imprint","IMPRINT",FACE,{"disambiguationData":[TD([[makeQuery(id+"F38.imprint","IMPRINT",EDGE,{"derivedFrom":sQuery(id+"F38.wireOp",EDGE,"E28")}),1.0]])]})])],"isStart":true});
            shell(context, id + "F58", {"entities" : qUnion([Q0, Q1]), "thickness" : 3 * mm});
        }
        {
            var Q0;
            Q0 = qSketchRegion(id + "F57", true);
            extrude(context, id + "F59", {"entities" : qUnion([Q0]), "operationType" : NewBodyOperationType.ADD, "depth" : 1 * mm, "offsetDistance" : 25 * mm, "hasSecondDirection" : true, "secondDirectionOppositeDirection" : true, "secondDirectionDepth" : 1 * mm});
        }
        {
            var Q0;
            Q0=makeQuery(id+"F59.opExtrude","CAP_EDGE",EDGE,{"disambiguationData":[OSD([sQuery(id+"F57.wireOp",EDGE,"E48")])],"isStart":false});
            var Q1;
            Q1=makeQuery(id+"F59.opExtrude","CAP_EDGE",EDGE,{"disambiguationData":[OSD([sQuery(id+"F57.wireOp",EDGE,"E48")])],"isStart":true});
            var Q2;
            Q2=makeQuery(id+"F59.opExtrude","CAP_EDGE",EDGE,{"disambiguationData":[OSD([sQuery(id+"F57.wireOp",EDGE,"E49")])],"isStart":false});
            var Q3;
            Q3=makeQuery(id+"F59.opExtrude","CAP_EDGE",EDGE,{"disambiguationData":[OSD([sQuery(id+"F57.wireOp",EDGE,"E49")])],"isStart":true});
            var Q4;
            Q4=makeQuery(id+"F59.opExtrude","CAP_EDGE",EDGE,{"disambiguationData":[OSD([sQuery(id+"F57.wireOp",EDGE,"E50")])],"isStart":false});
            var Q5;
            Q5=makeQuery(id+"F59.opExtrude","CAP_EDGE",EDGE,{"disambiguationData":[OSD([sQuery(id+"F57.wireOp",EDGE,"E50")])],"isStart":true});
            fillet(context, id + "F60", {"entities" : qUnion([Q0, Q1, Q2, Q3, Q4, Q5]), "radius" : 1 * mm, "tangentPropagation" : true, "allowEdgeOverflow" : false});
        }
        {
            var Q0;
            Q0=makeQuery(id+"F59.opExtrude","CAP_EDGE",EDGE,{"disambiguationData":[OSD([sQuery(id+"F57.wireOp",EDGE,"E43")])],"isStart":false});
            var Q1;
            Q1=makeQuery(id+"F59.opExtrude","CAP_EDGE",EDGE,{"disambiguationData":[OSD([sQuery(id+"F57.wireOp",EDGE,"E43")])],"isStart":true});
            var Q2;
            Q2=makeQuery(id+"F59.opExtrude","CAP_EDGE",EDGE,{"disambiguationData":[OSD([sQuery(id+"F57.wireOp",EDGE,"E42")])],"isStart":false});
            var Q3;
            Q3=makeQuery(id+"F59.opExtrude","CAP_EDGE",EDGE,{"disambiguationData":[OSD([sQuery(id+"F57.wireOp",EDGE,"E42")])],"isStart":true});
            fillet(context, id + "F61", {"entities" : qUnion([Q0, Q1, Q2, Q3]), "radius" : 1 * mm, "tangentPropagation" : true, "allowEdgeOverflow" : false});
        }
        {
            var Q0;
            Q0=sQuery(id+"F55.wireOp",EDGE,"E41");
            var Q1;
            Q1=qCreatedBy(id+"F37.planeOp",FACE);
            cPlane(context, id + "F62", {"entities" : qUnion([Q0, Q1]), "cplaneType" : CPlaneType.LINE_ANGLE, "offset" : 25 * mm, "angle" : 80 * degree, "width" : 150 * mm, "height" : 150 * mm});
        }
        {
            var Q0;
            Q0=qCreatedBy(id+"F62.planeOp",FACE);
            var sketch = newSketch(context, id + "F63", { "sketchPlane" : qUnion([Q0])});
            skLineSegment(sketch, "E51", {"start": v(-105.4, -289.37) * mm, "end": v(-194.08, -328.07) * mm});
            skLineSegment(sketch, "E52", {"start": v(-194.08, -328.07) * mm, "end": v(-217.33, -371.57) * mm});
            skLineSegment(sketch, "E53", {"start": v(-217.33, -371.57) * mm, "end": v(0, -331.06) * mm});
            skLineSegment(sketch, "E54", {"start": v(0, -331.06) * mm, "end": v(0, -245.65) * mm});
            skLineSegment(sketch, "E55", {"start": v(0, -245.65) * mm, "end": v(-105.4, -289.37) * mm});
            skLineSegment(sketch, "E56.MirrorCS", {"start": v(105.4, -289.37) * mm, "end": v(194.08, -328.07) * mm});
            skLineSegment(sketch, "E57.MirrorCS", {"start": v(0, -245.65) * mm, "end": v(105.4, -289.37) * mm});
            skLineSegment(sketch, "E58.MirrorCS", {"start": v(217.33, -371.57) * mm, "end": v(0, -331.06) * mm});
            skLineSegment(sketch, "E59.MirrorCS", {"start": v(194.08, -328.07) * mm, "end": v(217.33, -371.57) * mm});
            skSolve(sketch);
        }
        {
            var Q0;
            Q0=qCreatedBy(makeId("Top.planeOp"),FACE);
            cPlane(context, id + "F64", {"entities" : qUnion([Q0]), "cplaneType" : CPlaneType.OFFSET, "offset" : 430 * mm, "width" : 150 * mm, "height" : 150 * mm});
        }
        {
            var Q0;
            Q0=makeQuery(id+"F63.imprint","IMPRINT",FACE,{"disambiguationData":[TD([[makeQuery(id+"F63.imprint","IMPRINT",EDGE,{"derivedFrom":sQuery(id+"F63.wireOp",EDGE,"E51")}),1.0]])]});
            var Q1;
            Q1=makeQuery(id+"F63.imprint","IMPRINT",FACE,{"disambiguationData":[TD([[makeQuery(id+"F63.imprint","IMPRINT",EDGE,{"derivedFrom":sQuery(id+"F63.wireOp",EDGE,"E54")}),-1.0]])]});
            extrude(context, id + "F65", {"entities" : qUnion([Q0, Q1]), "operationType" : NewBodyOperationType.ADD, "depth" : 4 * mm, "offsetDistance" : 25 * mm});
        }
        {
            var Q0;
            Q0=makeQuery(id+"F65.opExtrude","CAP_EDGE",EDGE,{"disambiguationData":[OSD([sQuery(id+"F63.wireOp",EDGE,"E56.MirrorCS")])],"isStart":false});
            var Q1;
            {var subQ0=sQuery(id+"F63.wireOp",EDGE,"E59.MirrorCS");var subQ1=sQuery(id+"F63.wireOp",EDGE,"E58.MirrorCS");Q1=makeQuery(id+"F65.boolean.opBoolean","SPLIT",EDGE,{"disambiguationData":[TD([makeQuery(id+"F65.opExtrude","SWEPT_FACE",FACE,{"disambiguationData":[OSD([subQ0])]})])],"derivedFrom":makeQuery(id+"F65.opExtrude","CAP_EDGE",EDGE,{"disambiguationData":[OSD([subQ1])],"isStart":false})});}
            var Q2;
            Q2=makeQuery(id+"F65.opExtrude","CAP_EDGE",EDGE,{"disambiguationData":[OSD([sQuery(id+"F63.wireOp",EDGE,"E59.MirrorCS")])],"isStart":false});
            var Q3;
            Q3=makeQuery(id+"F65.opExtrude","CAP_EDGE",EDGE,{"disambiguationData":[OSD([sQuery(id+"F63.wireOp",EDGE,"E51")])],"isStart":false});
            var Q4;
            {var subQ0=sQuery(id+"F63.wireOp",EDGE,"E53");var subQ1=sQuery(id+"F63.wireOp",EDGE,"E52");Q4=makeQuery(id+"F65.boolean.opBoolean","SPLIT",EDGE,{"disambiguationData":[TD([makeQuery(id+"F65.opExtrude","SWEPT_FACE",FACE,{"disambiguationData":[OSD([subQ1])]})])],"derivedFrom":makeQuery(id+"F65.opExtrude","CAP_EDGE",EDGE,{"disambiguationData":[OSD([subQ0])],"isStart":false})});}
            var Q5;
            Q5=makeQuery(id+"F65.opExtrude","CAP_EDGE",EDGE,{"disambiguationData":[OSD([sQuery(id+"F63.wireOp",EDGE,"E52")])],"isStart":false});
            fillet(context, id + "F66", {"entities" : qUnion([Q0, Q1, Q2, Q3, Q4, Q5]), "radius" : 5 * mm, "tangentPropagation" : true, "allowEdgeOverflow" : false});
        }
        {
            var Q0;
            Q0 = qSketchRegion(id + "F45", true);
            var Q1;
            Q1=sQuery(id+"F45.wireOp",EDGE,"E33");
            revolve(context, id + "F67", {"surfaceOperationType" : NewSurfaceOperationType.NEW, "entities" : qUnion([Q0]), "axis" : qUnion([Q1]), "revolveType" : RevolveType.FULL});
        }
        {
            var Q0;
            Q0=makeQuery(id+"F67.opRevolve","SWEPT_BODY",BODY,{"disambiguationData":[OSD([sQuery(id+"F45.wireOp",EDGE,"E33"),sQuery(id+"F45.wireOp",EDGE,"E34"),sQuery(id+"F45.wireOp",EDGE,"E35"),sQuery(id+"F45.wireOp",EDGE,"E36")])]});
            transform(context, id + "F68", {"entities" : qUnion([Q0]), "transformType" : TransformType.TRANSLATION_3D, "dx" : 0 * mm, "dy" : -25 * mm, "dz" : 0 * mm, "makeCopy" : false});
        }
        {
            var Q0;
            Q0=makeQuery(id+"F67.opRevolve","SWEPT_BODY",BODY,{"disambiguationData":[OSD([sQuery(id+"F45.wireOp",EDGE,"E33"),sQuery(id+"F45.wireOp",EDGE,"E34"),sQuery(id+"F45.wireOp",EDGE,"E35"),sQuery(id+"F45.wireOp",EDGE,"E36")])]});
            transform(context, id + "F69", {"entities" : qUnion([Q0]), "transformType" : TransformType.TRANSLATION_3D, "dx" : 0 * mm, "dy" : 85.6 * mm, "dz" : 68.8 * mm, "makeCopy" : false});
        }
        {
            var Q0;
            Q0=makeQuery(id+"F67.opRevolve","SWEPT_BODY",BODY,{"disambiguationData":[OSD([sQuery(id+"F45.wireOp",EDGE,"E33"),sQuery(id+"F45.wireOp",EDGE,"E34"),sQuery(id+"F45.wireOp",EDGE,"E35"),sQuery(id+"F45.wireOp",EDGE,"E36")])]});
            transform(context, id + "F70", {"entities" : qUnion([Q0]), "transformType" : TransformType.TRANSLATION_3D, "dx" : 0 * mm, "dy" : -87 * mm, "dz" : -68.8 * mm, "makeCopy" : false});
        }
        {
            var Q0;
            Q0=makeQuery(id+"F32.opLoft","SWEPT_BODY",BODY,{"disambiguationData":[OSD([makeQuery(id+"F29.imprint","IMPRINT",FACE,{"disambiguationData":[TD([[makeQuery(id+"F29.imprint","IMPRINT",EDGE,{"derivedFrom":sQuery(id+"F29.wireOp",EDGE,"E23")}),-1.0]])]}),makeQuery(id+"F31.imprint","IMPRINT",FACE,{"disambiguationData":[TD([[makeQuery(id+"F31.imprint","IMPRINT",EDGE,{"derivedFrom":sQuery(id+"F31.wireOp",EDGE,"E25")}),-1.0]])]})])]});
            var Q1;
            Q1=makeQuery(id+"F24.opLoft","SWEPT_BODY",BODY,{"disambiguationData":[OSD([makeQuery(id+"F1.imprint","IMPRINT",FACE,{"disambiguationData":[TD([[makeQuery(id+"F1.imprint","IMPRINT",EDGE,{"derivedFrom":sQuery(id+"F1.wireOp",EDGE,"E1")}),-1.0]])]}),makeQuery(id+"F8.imprint","IMPRINT",FACE,{"disambiguationData":[TD([[makeQuery(id+"F8.imprint","IMPRINT",EDGE,{"derivedFrom":sQuery(id+"F8.wireOp",EDGE,"E6")}),-1.0]])]})])]});
            var Q2;
            Q2=makeQuery(id+"F21.opLoft","SWEPT_BODY",BODY,{"disambiguationData":[OSD([makeQuery(id+"F1.imprint","IMPRINT",FACE,{"disambiguationData":[TD([[makeQuery(id+"F1.imprint","IMPRINT",EDGE,{"derivedFrom":sQuery(id+"F1.wireOp",EDGE,"E1")}),-1.0]])]}),makeQuery(id+"F5.imprint","IMPRINT",FACE,{"disambiguationData":[TD([[makeQuery(id+"F5.imprint","IMPRINT",EDGE,{"derivedFrom":sQuery(id+"F5.wireOp",EDGE,"E3")}),-1.0]])]})])]});
            transform(context, id + "F71", {"entities" : qUnion([Q0, Q1, Q2]), "transformType" : TransformType.TRANSLATION_3D, "dx" : -404 * mm, "dy" : 213.3 * mm, "dz" : -306 * mm, "makeCopy" : false});
        }
        {
            var Q0;
            Q0=qCreatedBy(makeId("Right.planeOp"),FACE);
            var sketch = newSketch(context, id + "F72", { "sketchPlane" : qUnion([Q0])});
            skLineSegment(sketch, "E60", {"start": v(187.34, 0) * mm, "end": v(179.07, -17.34) * mm});
            skLineSegment(sketch, "E61", {"start": v(179.07, -17.34) * mm, "end": v(151.96, -17.34) * mm});
            skLineSegment(sketch, "E62", {"start": v(151.96, -17.34) * mm, "end": v(177.5, 0) * mm});
            skLineSegment(sketch, "E63", {"start": v(177.5, 0) * mm, "end": v(187.34, 0) * mm});
            skSolve(sketch);
        }
        {
            var Q0;
            Q0 = qSketchRegion(id + "F72", true);
            extrude(context, id + "F73", {"entities" : qUnion([Q0]), "operationType" : NewBodyOperationType.REMOVE, "oppositeDirection" : true, "depth" : 25 * mm, "offsetDistance" : 25 * mm, "hasSecondDirection" : true, "secondDirectionOppositeDirection" : false, "secondDirectionDepth" : 25 * mm});
        }
    });
